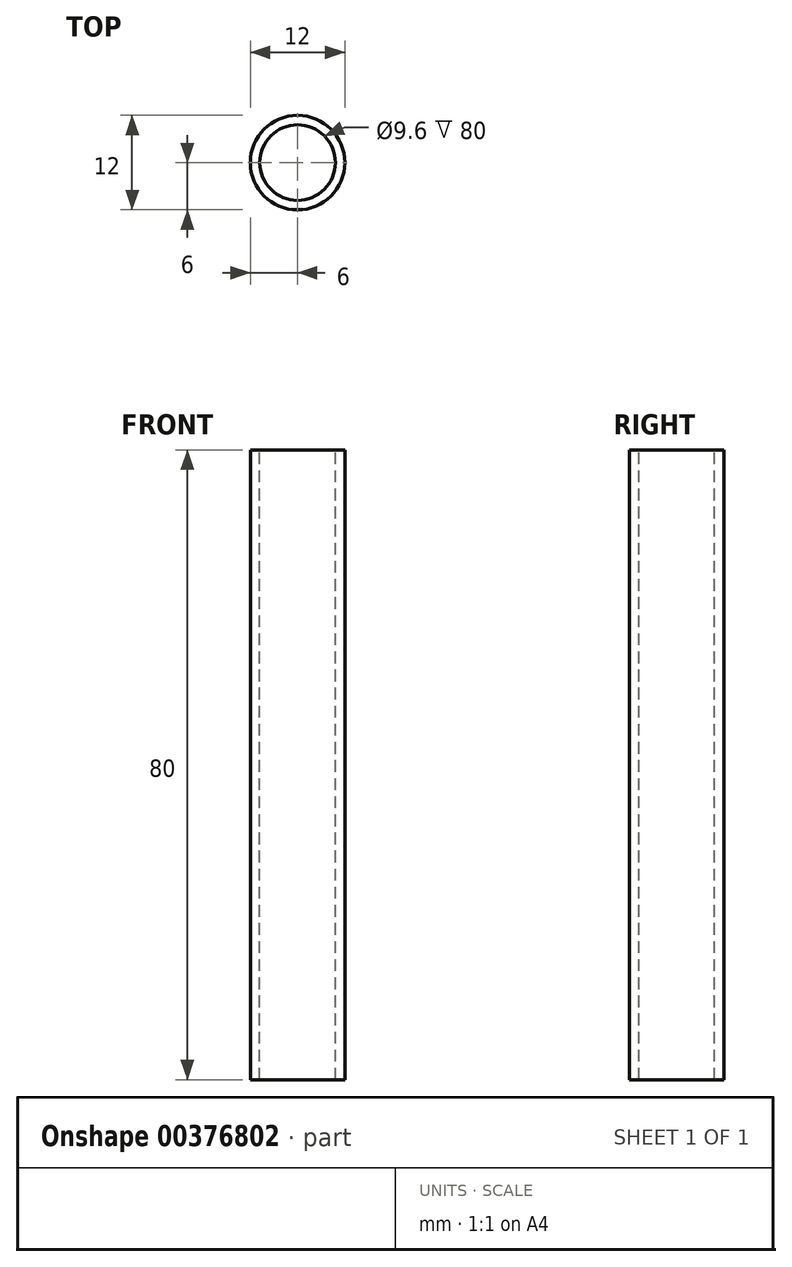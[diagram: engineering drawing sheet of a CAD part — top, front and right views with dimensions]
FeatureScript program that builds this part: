
annotation { "Feature Type Name" : "Feature", "Feature Type Description" : "" }
export const myFeature = defineFeature(function(context is Context, id is Id, definition is map)
    precondition{}
    {
        {
            var Q0;
            Q0=qCreatedBy(makeId("Front.planeOp"),FACE);
            var sketch = newSketch(context, id + "F0", { "sketchPlane" : qUnion([Q0])});
            skLineSegment(sketch, "E0", {"start": v(6, 74.7) * mm, "end": v(6, -5.3) * mm});
            skLineSegment(sketch, "E1", {"start": v(6, -5.3) * mm, "end": v(4.8, -5.3) * mm});
            skLineSegment(sketch, "E2", {"start": v(4.8, -5.3) * mm, "end": v(4.8, 74.7) * mm});
            skLineSegment(sketch, "E3", {"start": v(4.8, 74.7) * mm, "end": v(6, 74.7) * mm});
            skLineSegment(sketch, "E4", {"start": v(0, 16.8) * mm, "end": v(0, -13.13) * mm, "construction": true});
            skSolve(sketch);
        }
        {
            var Q0;
            Q0=makeQuery(id+"F0.imprint","IMPRINT",FACE,{"disambiguationData":[TD([[makeQuery(id+"F0.imprint","IMPRINT",EDGE,{"derivedFrom":sQuery(id+"F0.wireOp",EDGE,"E0")}),-1.0]])]});
            var Q1;
            Q1=sQuery(id+"F0.wireOp",EDGE,"E4");
            revolve(context, id + "F1", {"entities" : qUnion([Q0]), "axis" : qUnion([Q1]), "revolveType" : RevolveType.FULL});
        }
    });
